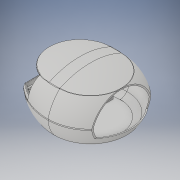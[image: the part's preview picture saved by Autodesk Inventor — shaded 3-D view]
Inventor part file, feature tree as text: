
AUTODESK INVENTOR PART (.ipt)
format: ipt  version: 2019 (Build 230136000, 136)  size: 2,721,792 bytes
history: native  units: mm
features: sketch x33, other x31, extrude x15, loft x12, pattern_linear x12, projected_geometry x12, fillet x10, mirror x5, revolve x3
ambient origin geometry x8: Origin, YZ Plane, XZ Plane, XY Plane, X Axis, Y Axis, Z Axis, Center Point
bodies: Body1 (feature_tree), Body2 (feature_tree)
feature tree (133):
  other  "голова"
  other  "Твердое тело1"
  sketch  "Эскиз1"
  extrude  "Выдавливание1"  Depth=42.3mm
  extrude  "Выдавливание2"  Depth=20.3mm
  extrude  "Выдавливание3"  Depth=40.0mm
  other  "РабПлоскость1"
  sketch  "Эскиз3"
  other  "РабПлоскость2"
  loft  "Лофт1"
  other  "РабПлоскость3"
  sketch  "Эскиз5"
  loft  "Лофт3"
  other  "РабПлоскость4"
  sketch  "Эскиз8"
  other  "РабПлоскость6"
  sketch  "Эскиз9"
  loft  "Лофт4"
  extrude  "Выдавливание4"  Depth=100.0mm
  mirror  "Зеркальное отражение1"
  loft  "Лофт5"
  loft  "Лофт6"
  loft  "Лофт7"
  sketch  "Эскиз11"
  extrude  "Выдавливание5"  Depth=20.0mm
  mirror  "Зеркальное отражение2"
  sketch  "Эскиз13"
  other  "РабПлоскость7"
  sketch  "Эскиз14"
  other  "РабПлоскость9"
  sketch  "Эскиз16"
  other  "РабПлоскость10"
  sketch  "Эскиз17"
  other  "РабПлоскость8"
  extrude  "Выдавливание6"  Depth=2.0mm TaperAngle=0.0deg
  loft  "Лофт8"
  mirror  "Зеркальное отражение3"
  other  "РабПлоскость11"
  revolve  "Вращение1"
  extrude  "Выдавливание7"  Depth=2.0mm
  loft  "Лофт9"
  loft  "Лофт10"
  other  "РабПлоскость12"
  sketch  "Эскиз20"
  sketch  "Эскиз21"
  sketch  "Эскиз22"
  loft  "Лофт11"
  loft  "Лофт12"
  mirror  "Зеркальное отражение4"
  other  "РабПлоскость13"
  loft  "Лофт13"
  extrude  "Выдавливание9"  Depth=50.0mm
  fillet  "Сопряжение1"  Radius=52.0mm
  fillet  "Сопряжение2"  Radius=2.0mm
  fillet  "Сопряжение3"  Radius=2.0mm
  fillet  "Сопряжение4"  Radius=46.0mm
  fillet  "Сопряжение5"  Radius=31.0mm
  fillet  "Сопряжение6"  Radius=30.0mm
  fillet  "Сопряжение7"  Radius=2.0mm
  extrude  "Выдавливание10"  Depth=2.0mm
  pattern_linear  "Прямоуг.массив1"  Spacing1=2.0mm  [1 undecoded]
  pattern_linear  "Прямоуг.массив2"  Spacing1=98.851581mm  [1 undecoded]
  pattern_linear  "Прямоуг.массив3"  Spacing1=40.790396mm  [1 undecoded]
  pattern_linear  "Прямоуг.массив4"  Spacing1=0.0mm  [1 undecoded]
  pattern_linear  "Прямоуг.массив5"  Spacing1=0.0mm  [1 undecoded]
  pattern_linear  "Прямоуг.массив6"  Spacing1=2.0mm  [1 undecoded]
  pattern_linear  "Прямоуг.массив7"  Spacing1=2.0mm  [1 undecoded]
  pattern_linear  "Прямоуг.массив8"  Spacing1=2.0mm  [1 undecoded]
  pattern_linear  "Прямоуг.массив9"  Spacing1=83.118457mm  [1 undecoded]
  pattern_linear  "Прямоуг.массив10"  Spacing1=1.99778mm  [1 undecoded]
  pattern_linear  "Прямоуг.массив11"  Spacing1=0.0mm  [1 undecoded]
  pattern_linear  "Прямоуг.массив12"  Spacing1=0.0mm  [1 undecoded]
  mirror  "Зеркальное отражение5"
  fillet  "Сопряжение8"  Radius=2.0mm
  fillet  "Сопряжение9"  Radius=2.0mm
  fillet  "Сопряжение10"  Radius=2.0mm
  extrude  "Выдавливание12"  Depth=53.0mm
  revolve  "Вращение2"
  extrude  "Выдавливание13"  Depth=2.0mm
  revolve  "Вращение3"
  other  "РабПлоскость14"
  sketch  "Эскиз35"
  extrude  "Выдавливание14"  TaperAngle=0.0deg  [1 undecoded]
  extrude  "Выдавливание15"  TaperAngle=0.0deg  [1 undecoded]
  extrude  "Выдавливание16"  TaperAngle=0.0deg  [1 undecoded]
  other  "РабПлоскость15"
  extrude  "Выдавливание17"  Depth=60.0mm TaperAngle=0.0deg
  sketch  "Эскиз2"
  sketch  "Эскиз4"
  projected_geometry  "Спроецированная петля1"
  other  "Ребра2"
  projected_geometry  "Спроецированная петля2"
  other  "Ребра3"
  other  "Ребра1"
  sketch  "Эскиз10"
  projected_geometry  "Спроецированная петля3"
  other  "Ребра4"
  other  "Ребра5"
  other  "Ребра6"
  other  "Ребра7"
  other  "Ребра8"
  other  "Ребра9"
  sketch  "Эскиз12"
  projected_geometry  "Спроецированная петля4"
  sketch  "Эскиз15"
  projected_geometry  "Спроецированная петля5"
  other  "Ребра10"
  sketch  "Эскиз18"
  sketch  "Эскиз19"
  projected_geometry  "Спроецированная петля6"
  other  "Ребра11"
  other  "Ребра12"
  other  "Ребра13"
  other  "Ребра14"
  projected_geometry  "Спроецированная петля7"
  projected_geometry  "Спроецированная петля8"
  other  "Ребра15"
  sketch  "Эскиз24"
  sketch  "Эскиз25"
  projected_geometry  "Спроецированная петля10"
  sketch  "Эскиз26"
  sketch  "Эскиз27"
  sketch  "Эскиз29"
  sketch  "Эскиз32"
  projected_geometry  "Спроецированная петля11"
  sketch  "Эскиз33"
  sketch  "Эскиз34"
  sketch  "Эскиз37"
  sketch  "Эскиз38"
  sketch  "Эскиз39"
  projected_geometry  "Спроецированная петля12"
  projected_geometry  "Спроецированная петля13"
  sketch  "Эскиз40"
note: 15 required parameter values undecoded (feature->parameter linkage not recoverable at this tier; creation-order binding heuristic only, values carry confidence <= 0.55)
